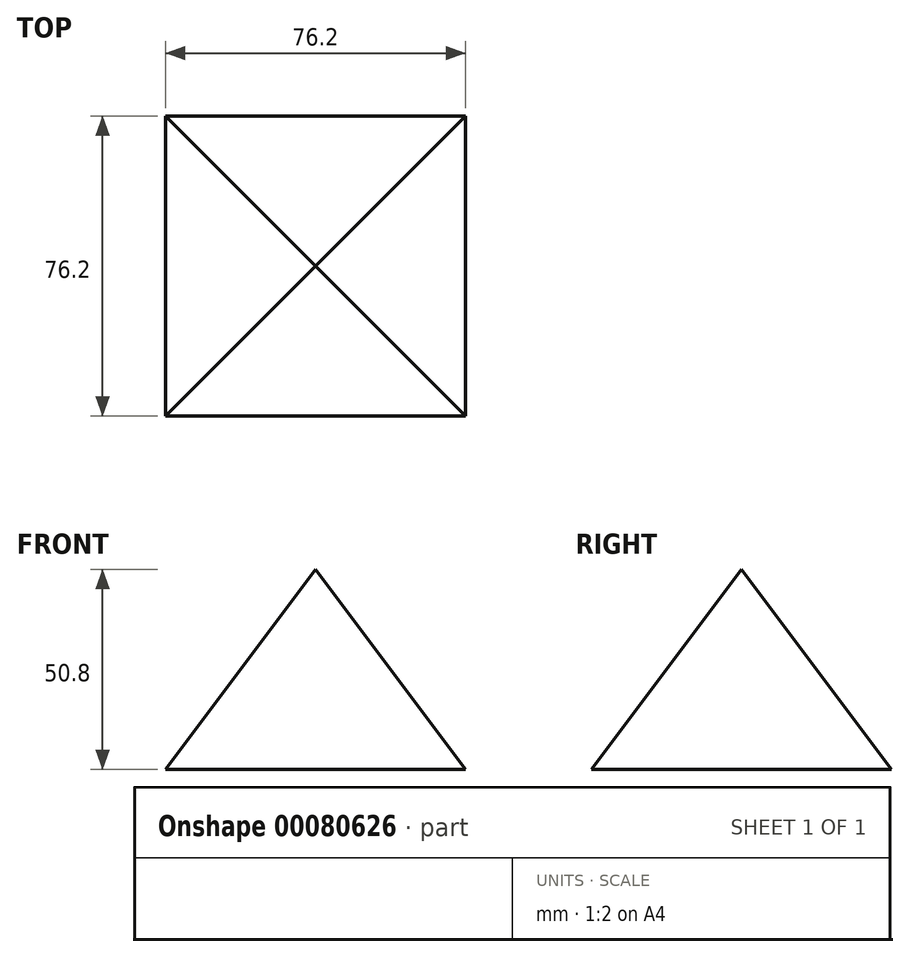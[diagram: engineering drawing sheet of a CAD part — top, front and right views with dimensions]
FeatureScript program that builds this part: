
annotation { "Feature Type Name" : "Feature", "Feature Type Description" : "" }
export const myFeature = defineFeature(function(context is Context, id is Id, definition is map)
    precondition{}
    {
        {
            var Q0;
            Q0=qCreatedBy(makeId("Top.planeOp"),FACE);
            var sketch = newSketch(context, id + "F0", { "sketchPlane" : qUnion([Q0])});
            skLineSegment(sketch, "E0.bottom", {"start": v(-38.1, 38.1) * mm, "end": v(38.1, 38.1) * mm});
            skLineSegment(sketch, "E0.top", {"start": v(-38.1, -38.1) * mm, "end": v(38.1, -38.1) * mm});
            skLineSegment(sketch, "E0.left", {"start": v(-38.1, 38.1) * mm, "end": v(-38.1, -38.1) * mm});
            skLineSegment(sketch, "E0.right", {"start": v(38.1, 38.1) * mm, "end": v(38.1, -38.1) * mm});
            skPoint(sketch, "E0.middle", {"position": v(0, 0) * mm});
            skSolve(sketch);
        }
        {
            var Q0;
            Q0=qCreatedBy(makeId("Front.planeOp"),FACE);
            var sketch = newSketch(context, id + "F1", { "sketchPlane" : qUnion([Q0])});
            skLineSegment(sketch, "E1", {"start": v(0, 0) * mm, "end": v(0, 50.8) * mm});
            skLineSegment(sketch, "E2", {"start": v(0, 50.8) * mm, "end": v(-38.1, 0) * mm});
            skSolve(sketch);
        }
        {
            var Q0;
            Q0=makeQuery(id+"F0.imprint","IMPRINT",FACE,{"disambiguationData":[TD([[makeQuery(id+"F0.imprint","IMPRINT",EDGE,{"derivedFrom":sQuery(id+"F0.wireOp",EDGE,"E0.bottom")}),-1.0]])]});
            var Q1;
            Q1=sQuery(id+"F1.wireOp",VERTEX,"E2.start");
            loft(context, id + "F2", {"sheetProfilesArray" : [{ "sheetProfileEntities" : qUnion([Q0]) }, { "sheetProfileEntities" : qUnion([Q1]) }]});
        }
    });
